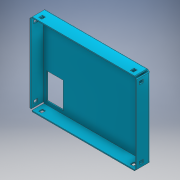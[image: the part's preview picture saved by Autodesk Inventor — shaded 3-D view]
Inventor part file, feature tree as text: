
AUTODESK INVENTOR PART (.ipt)
format: ipt  version: 2018 (Build 220112000, 112)  size: 242,688 bytes
history: native  units: mm
features: extrude x5, sketch x5, fillet x1
ambient origin geometry x8: Origin, YZ Plane, XZ Plane, XY Plane, X Axis, Y Axis, Z Axis, Center Point
bodies: Body1 (feature_tree)
feature tree (11):
  extrude  "Extrusion3"  Depth=2.0mm
  extrude  "Extrusion5"  Depth=2.0mm
  extrude  "Extrusion6"  Depth=0.5mm
  extrude  "Extrusion7"  Depth=0.5mm
  extrude  "Extrusion8"  Depth=0.5mm TaperAngle=0.0deg
  fillet  "Fillet1"  Radius=1.4mm
  sketch  "Sketch3"  dims[d21=2.0mm d22=2.0mm]
  sketch  "Sketch6"  dims[d23=2.0mm d24=2.0mm]
  sketch  "Sketch7"  dims[d31=0.5mm d32=0.0mm d45=0.5mm]
  sketch  "Sketch8"  dims[d46=0.5mm d48=2.0mm]
  sketch  "Sketch9"  dims[d49=0.5mm d50=5.5mm d51=0.0mm d52=1.4mm d53=1.7mm d54=3.1mm d55=1.7mm d56=1.4mm d57=1.7mm d58=3.1mm d59=1.7mm d60=5.5mm d61=0.0mm d62=1.4mm d63=1.7mm d64=3.1mm d65=1.2mm d66=1.4mm d67=1.7mm d68=3.1mm d69=1.2mm d70=5.5mm d71=0.0mm d74=7.5mm d75=11.8mm d76=2.0mm d77=2.0mm d78=5.5mm d79=0.0mm d80=0.5mm]
